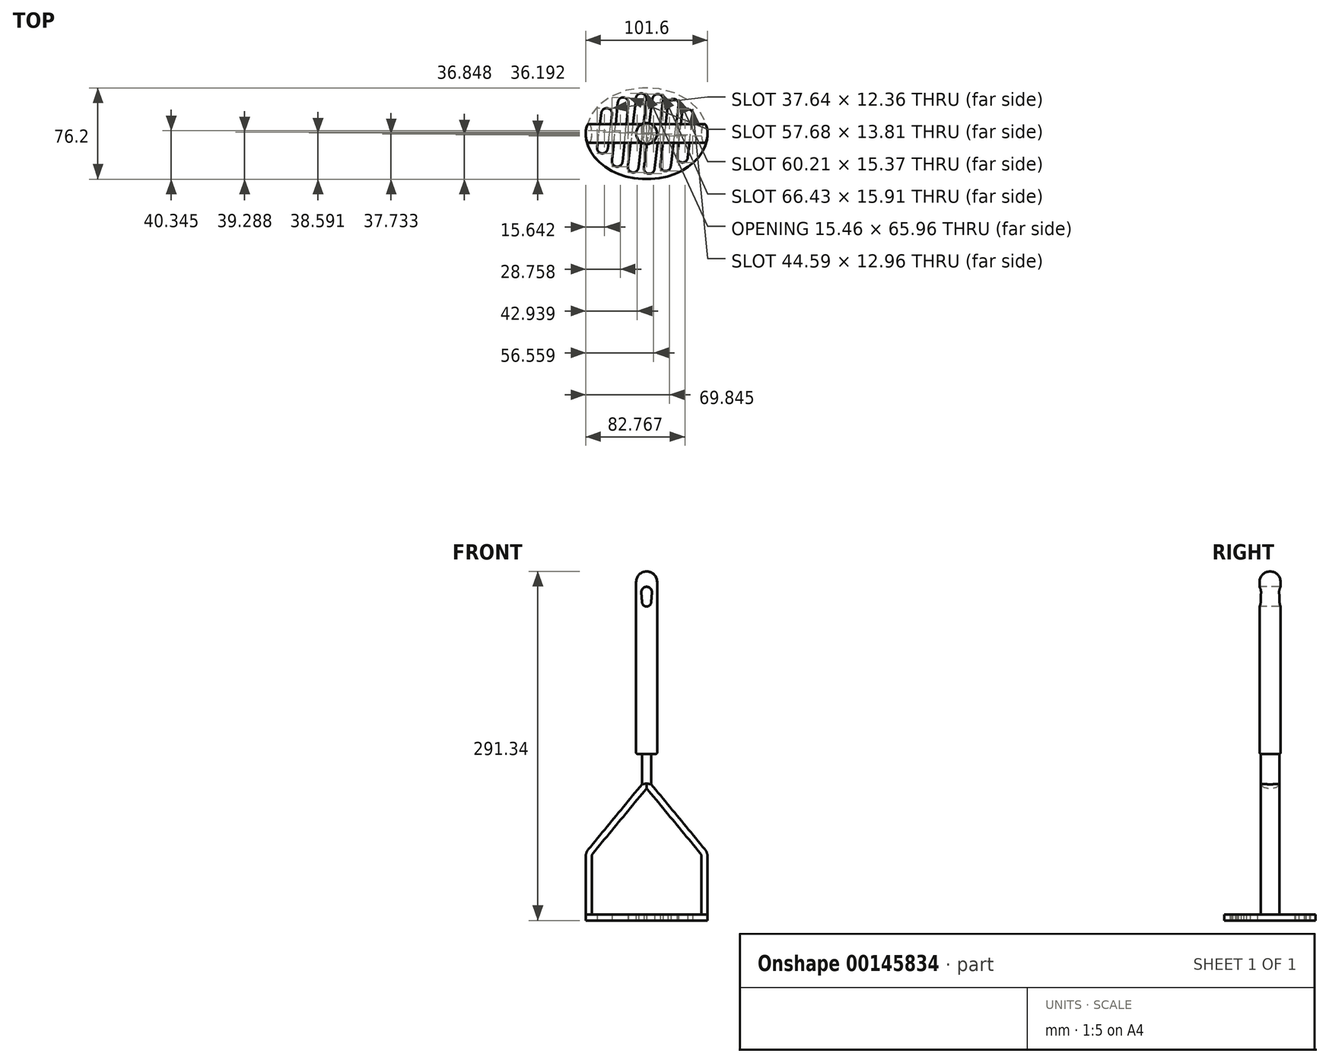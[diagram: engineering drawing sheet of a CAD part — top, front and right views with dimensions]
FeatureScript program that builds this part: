
annotation { "Feature Type Name" : "Feature", "Feature Type Description" : "" }
export const myFeature = defineFeature(function(context is Context, id is Id, definition is map)
    precondition{}
    {
        {
            var Q0;
            Q0=qCreatedBy(makeId("Top.planeOp"),FACE);
            var sketch = newSketch(context, id + "F0", { "sketchPlane" : qUnion([Q0])});
            skEllipse(sketch, "E0", {"center": v(0, 0) * mm, "majorRadius": 50.8 * mm, "minorRadius": 38.1 * mm, "majorAxis": v(1, 0)});
            skSolve(sketch);
        }
        {
            var Q0;
            Q0 = qSketchRegion(id + "F0", true);
            var Q1;
            Q1=makeQuery(id+"F0.imprint","IMPRINT",FACE,{"disambiguationData":[TD([[makeQuery(id+"F0.imprint","IMPRINT",EDGE,{"derivedFrom":sQuery(id+"F0.wireOp",EDGE,"E0")}),1.0]])]});
            extrude(context, id + "F1", {"entities" : qUnion([Q0, Q1]), "depth" : 5.08 * mm});
        }
        {
            var Q0;
            Q0=qCreatedBy(makeId("Right.planeOp"),FACE);
            var sketch = newSketch(context, id + "F2", { "sketchPlane" : qUnion([Q0])});
            skLineSegment(sketch, "E1", {"start": v(0, 0) * mm, "end": v(0, 114.3) * mm});
            skSolve(sketch);
        }
        {
            var Q0;
            Q0=makeQuery(id+"F1.opExtrude","CAP_FACE",FACE,{"disambiguationData":[OSD([sQuery(id+"F0.wireOp",EDGE,"E0")])],"isStart":false});
            var sketch = newSketch(context, id + "F3", { "sketchPlane" : qUnion([Q0])});
            skEllipse(sketch, "E2.0", {"center": v(0, 0) * mm, "majorRadius": 50.8 * mm, "minorRadius": 38.1 * mm, "majorAxis": v(1, 0)});
            skLineSegment(sketch, "E3", {"start": v(-50.8, 0) * mm, "end": v(-48.26, 0) * mm});
            skEllipse(sketch, "E4", {"center": v(-48.26, 0) * mm, "majorRadius": 2.54 * mm, "minorRadius": 7.89 * mm, "majorAxis": v(-1, 0)});
            skSolve(sketch);
        }
        {
            var Q0;
            Q0=qCreatedBy(makeId("Front.planeOp"),FACE);
            var sketch = newSketch(context, id + "F4", { "sketchPlane" : qUnion([Q0])});
            skLineSegment(sketch, "E5.0", {"start": v(-50.8, 5.08) * mm, "end": v(-45.72, 5.08) * mm});
            skLineSegment(sketch, "E6", {"start": v(-48.26, 5.08) * mm, "end": v(-48.26, 53.6) * mm});
            skLineSegment(sketch, "E7.0", {"start": v(0, 0) * mm, "end": v(0, 114.3) * mm});
            skLineSegment(sketch, "E8", {"start": v(-46.8, 57.64) * mm, "end": v(0, 114.3) * mm});
            skPoint(sketch, "E9.visualSharp", {"position": v(-48.26, 55.88) * mm});
            skArc(sketch, "E9.filletArc", {"start": v(-46.8, 57.64) * mm, "mid": v(-47.89, 55.75) * mm, "end": v(-48.26, 53.6) * mm});
            skSolve(sketch);
        }
        {
            var Q0;
            Q0=makeQuery(id+"F3.imprint","IMPRINT",FACE,{"disambiguationData":[TD([[makeQuery(id+"F3.imprint","IMPRINT",EDGE,{"derivedFrom":sQuery(id+"F3.wireOp",EDGE,"E4")}),1.0]])]});
            var Q1;
            Q1=sQuery(id+"F4.wireOp",EDGE,"E6");
            var Q2;
            Q2=sQuery(id+"F4.wireOp",EDGE,"E9.filletArc");
            var Q3;
            Q3=sQuery(id+"F4.wireOp",EDGE,"E8");
            sweep(context, id + "F5", {"operationType" : NewBodyOperationType.ADD, "profiles" : qUnion([Q0]), "path" : qUnion([Q1, Q2, Q3])});
        }
        {
            var Q0;
            Q0=makeQuery(id+"F1.opExtrude","CAP_FACE",FACE,{"disambiguationData":[OSD([sQuery(id+"F0.wireOp",EDGE,"E0")])],"isStart":false});
            var sketch = newSketch(context, id + "F6", { "sketchPlane" : qUnion([Q0])});
            skEllipse(sketch, "E10.0", {"center": v(0, 0) * mm, "majorRadius": 50.8 * mm, "minorRadius": 38.1 * mm, "majorAxis": v(1, 0)});
            skLineSegment(sketch, "E11", {"start": v(50.8, 0) * mm, "end": v(48.26, 0) * mm});
            skPoint(sketch, "E11.endSnap0", {"position": v(50.8, 0) * mm});
            skEllipse(sketch, "E12", {"center": v(48.26, 0) * mm, "majorRadius": 2.54 * mm, "minorRadius": 7.87 * mm, "majorAxis": v(1, 0)});
            skSolve(sketch);
        }
        {
            var Q0;
            Q0=qCreatedBy(makeId("Front.planeOp"),FACE);
            var sketch = newSketch(context, id + "F7", { "sketchPlane" : qUnion([Q0])});
            skLineSegment(sketch, "E13.0", {"start": v(50.8, 5.08) * mm, "end": v(45.72, 5.08) * mm});
            skLineSegment(sketch, "E14.0", {"start": v(0, 0) * mm, "end": v(0, 114.3) * mm});
            skLineSegment(sketch, "E15", {"start": v(48.26, 5.08) * mm, "end": v(48.26, 53.6) * mm});
            skLineSegment(sketch, "E16", {"start": v(46.8, 57.64) * mm, "end": v(0, 114.3) * mm});
            skPoint(sketch, "E17.visualSharp", {"position": v(48.26, 55.88) * mm});
            skArc(sketch, "E17.filletArc", {"start": v(48.26, 53.6) * mm, "mid": v(47.89, 55.75) * mm, "end": v(46.8, 57.64) * mm});
            skSolve(sketch);
        }
        {
            var Q0;
            Q0=makeQuery(id+"F6.imprint","IMPRINT",FACE,{"disambiguationData":[TD([[makeQuery(id+"F6.imprint","IMPRINT",EDGE,{"derivedFrom":sQuery(id+"F6.wireOp",EDGE,"E12")}),1.0]])]});
            var Q1;
            Q1=sQuery(id+"F7.wireOp",EDGE,"E15");
            var Q2;
            Q2=sQuery(id+"F7.wireOp",EDGE,"E17.filletArc");
            var Q3;
            Q3=sQuery(id+"F7.wireOp",EDGE,"E16");
            sweep(context, id + "F8", {"operationType" : NewBodyOperationType.ADD, "profiles" : qUnion([Q0]), "path" : qUnion([Q1, Q2, Q3])});
        }
        {
            var Q0;
            Q0=makeQuery(id+"F0.imprint","IMPRINT",FACE,{"disambiguationData":[TD([[makeQuery(id+"F0.imprint","IMPRINT",EDGE,{"derivedFrom":sQuery(id+"F0.wireOp",EDGE,"E0")}),1.0]])]});
            cPlane(context, id + "F9", {"entities" : qUnion([Q0]), "cplaneType" : CPlaneType.OFFSET, "offset" : 113.54 * mm, "width" : 152.4 * mm, "height" : 152.4 * mm});
        }
        {
            var Q0;
            Q0=qCreatedBy(id+"F9.planeOp",FACE);
            var sketch = newSketch(context, id + "F10", { "sketchPlane" : qUnion([Q0])});
            skEllipse(sketch, "E18", {"center": v(0, 0) * mm, "majorRadius": 3.81 * mm, "minorRadius": 7.87 * mm, "majorAxis": v(1, 0)});
            skSolve(sketch);
        }
        {
            var Q0;
            Q0 = qSketchRegion(id + "F10", true);
            extrude(context, id + "F11", {"entities" : qUnion([Q0]), "operationType" : NewBodyOperationType.ADD, "depth" : 25.4 * mm});
        }
        {
            var Q0;
            Q0=makeQuery(id+"F11.opExtrude","CAP_FACE",FACE,{"disambiguationData":[OSD([sQuery(id+"F10.wireOp",EDGE,"E18")])],"isStart":false});
            var sketch = newSketch(context, id + "F12", { "sketchPlane" : qUnion([Q0])});
            skCircle(sketch, "E19", {"center": v(0, 0) * mm, "radius": 8.76 * mm});
            skSolve(sketch);
        }
        {
            var Q0;
            Q0 = qSketchRegion(id + "F12", true);
            extrude(context, id + "F13", {"entities" : qUnion([Q0]), "depth" : 152.4 * mm});
        }
        {
            var Q0;
            Q0=makeQuery(id+"F13.opExtrude","CAP_EDGE",EDGE,{"disambiguationData":[OSD([sQuery(id+"F12.wireOp",EDGE,"E19")])],"isStart":false});
            fillet(context, id + "F14", {"entities" : qUnion([Q0]), "radius" : 8.76 * mm, "tangentPropagation" : true, "allowEdgeOverflow" : false});
        }
        {
            var Q0;
            Q0=qCreatedBy(makeId("Front.planeOp"),FACE);
            var sketch = newSketch(context, id + "F15", { "sketchPlane" : qUnion([Q0])});
            skArc(sketch, "E20", {"start": v(4.43, 273.71) * mm, "mid": v(0, 278.5) * mm, "end": v(-4.43, 273.71) * mm});
            skArc(sketch, "E21", {"start": v(-3.8, 265.5) * mm, "mid": v(0, 261.98) * mm, "end": v(3.8, 265.5) * mm});
            skLineSegment(sketch, "E22", {"start": v(-3.8, 265.5) * mm, "end": v(-4.43, 273.71) * mm});
            skLineSegment(sketch, "E23", {"start": v(3.8, 265.5) * mm, "end": v(4.43, 273.71) * mm});
            skSolve(sketch);
        }
        {
            var Q0;
            Q0 = qSketchRegion(id + "F15", true);
            extrude(context, id + "F16", {"entities" : qUnion([Q0]), "operationType" : NewBodyOperationType.REMOVE, "endBound" : BoundingType.SYMMETRIC, "oppositeDirection" : true, "depth" : 17.78 * mm});
        }
        {
            var Q0;
            Q0=makeQuery(id+"F0.imprint","IMPRINT",FACE,{"disambiguationData":[TD([[makeQuery(id+"F0.imprint","IMPRINT",EDGE,{"derivedFrom":sQuery(id+"F0.wireOp",EDGE,"E0")}),1.0]])]});
            var sketch = newSketch(context, id + "F17", { "sketchPlane" : qUnion([Q0])});
            skArc(sketch, "E24", {"start": v(-41.12, -10.8) * mm, "mid": v(-37.89, -16.56) * mm, "end": v(-32.5, -12.73) * mm});
            skArc(sketch, "E25", {"start": v(-28.98, 16.11) * mm, "mid": v(-32.86, 21.07) * mm, "end": v(-37.8, 17.18) * mm});
            skLineSegment(sketch, "E26", {"start": v(-41.34, -12.62) * mm, "end": v(-37.8, 17.18) * mm});
            skLineSegment(sketch, "E27", {"start": v(-32.5, -12.78) * mm, "end": v(-28.98, 16.11) * mm});
            skArc(sketch, "E28", {"start": v(-28.88, -22.2) * mm, "mid": v(-25.33, -27.65) * mm, "end": v(-20.14, -23.72) * mm});
            skArc(sketch, "E29", {"start": v(-15.14, 25.15) * mm, "mid": v(-19.1, 30.03) * mm, "end": v(-23.98, 26.05) * mm});
            skLineSegment(sketch, "E30", {"start": v(-28.88, -22.2) * mm, "end": v(-23.98, 26.05) * mm});
            skLineSegment(sketch, "E31", {"start": v(-20.14, -23.72) * mm, "end": v(-15.14, 25.15) * mm});
            skArc(sketch, "E32", {"start": v(-15.58, -27.11) * mm, "mid": v(-11.72, -32.49) * mm, "end": v(-6.8, -28.07) * mm});
            skArc(sketch, "E33", {"start": v(-0.13, 28.5) * mm, "mid": v(-4.55, 33.47) * mm, "end": v(-8.96, 28.5) * mm});
            skLineSegment(sketch, "E34", {"start": v(-8.96, 28.5) * mm, "end": v(-15.53, -26.52) * mm});
            skArc(sketch, "E35", {"start": v(-2.14, -28.1) * mm, "mid": v(1.63, -33.58) * mm, "end": v(6.62, -29.17) * mm});
            skArc(sketch, "E36", {"start": v(13.71, 27.89) * mm, "mid": v(9.85, 32.85) * mm, "end": v(4.9, 28.98) * mm});
            skLineSegment(sketch, "E37", {"start": v(-6.8, -28.07) * mm, "end": v(0, 29.6) * mm});
            skArc(sketch, "E38", {"start": v(11.36, -26.35) * mm, "mid": v(15.5, -31.36) * mm, "end": v(20.21, -26.88) * mm});
            skArc(sketch, "E39", {"start": v(26.73, 23.84) * mm, "mid": v(22.3, 28.85) * mm, "end": v(17.92, 23.82) * mm});
            skLineSegment(sketch, "E40", {"start": v(18.22, 26.11) * mm, "end": v(11.36, -26.35) * mm});
            skLineSegment(sketch, "E41", {"start": v(20.21, -26.88) * mm, "end": v(26.73, 23.84) * mm});
            skArc(sketch, "E42", {"start": v(25.49, -19.7) * mm, "mid": v(29.94, -24.2) * mm, "end": v(34.38, -19.7) * mm});
            skArc(sketch, "E43", {"start": v(38.44, 15.46) * mm, "mid": v(34.54, 20.38) * mm, "end": v(29.61, 16.47) * mm});
            skLineSegment(sketch, "E44", {"start": v(25.49, -19.7) * mm, "end": v(29.61, 16.47) * mm});
            skLineSegment(sketch, "E45", {"start": v(34.38, -19.7) * mm, "end": v(38.44, 15.46) * mm});
            skLineSegment(sketch, "E46", {"start": v(4.9, 28.98) * mm, "end": v(-2.14, -28.1) * mm});
            skLineSegment(sketch, "E47", {"start": v(13.71, 27.89) * mm, "end": v(6.62, -29.17) * mm});
            skLineSegment(sketch, "E48", {"start": v(-15.53, -26.52) * mm, "end": v(-15.58, -27.11) * mm});
            skSolve(sketch);
        }
        {
            var Q0;
            Q0 = qSketchRegion(id + "F17", true);
            extrude(context, id + "F18", {"entities" : qUnion([Q0]), "operationType" : NewBodyOperationType.REMOVE, "depth" : 5.08 * mm});
        }
        {
            var Q0;
            Q0=makeQuery(id+"F13.opExtrude","CAP_EDGE",EDGE,{"disambiguationData":[OSD([sQuery(id+"F12.wireOp",EDGE,"E19")])],"isStart":true});
            fillet(context, id + "F19", {"entities" : qUnion([Q0]), "radius" : 1.27 * mm, "tangentPropagation" : true, "allowEdgeOverflow" : false});
        }
    });
